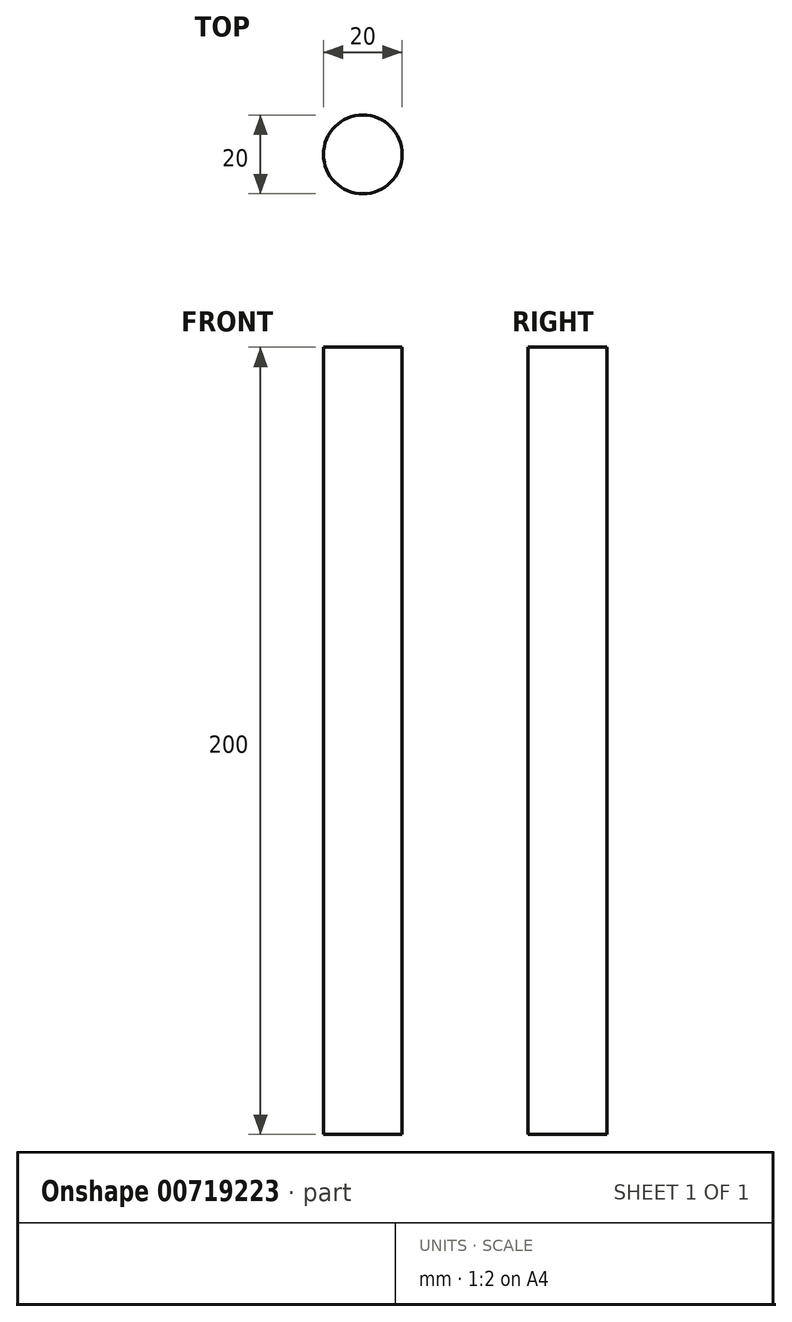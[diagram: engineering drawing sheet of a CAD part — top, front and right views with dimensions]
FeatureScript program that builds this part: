
annotation { "Feature Type Name" : "Feature", "Feature Type Description" : "" }
export const myFeature = defineFeature(function(context is Context, id is Id, definition is map)
    precondition{}
    {
        {
            var Q0;
            Q0=qCreatedBy(makeId("Top.planeOp"),FACE);
            var sketch = newSketch(context, id + "F0", { "sketchPlane" : qUnion([Q0])});
            skCircle(sketch, "E0", {"center": v(0, 0) * mm, "radius": 10 * mm});
            skSolve(sketch);
        }
        {
            var Q0;
            Q0 = qSketchRegion(id + "F0", true);
            extrude(context, id + "F1", {"entities" : qUnion([Q0]), "depth" : 200 * mm, "offsetDistance" : 25 * mm});
        }
    });
